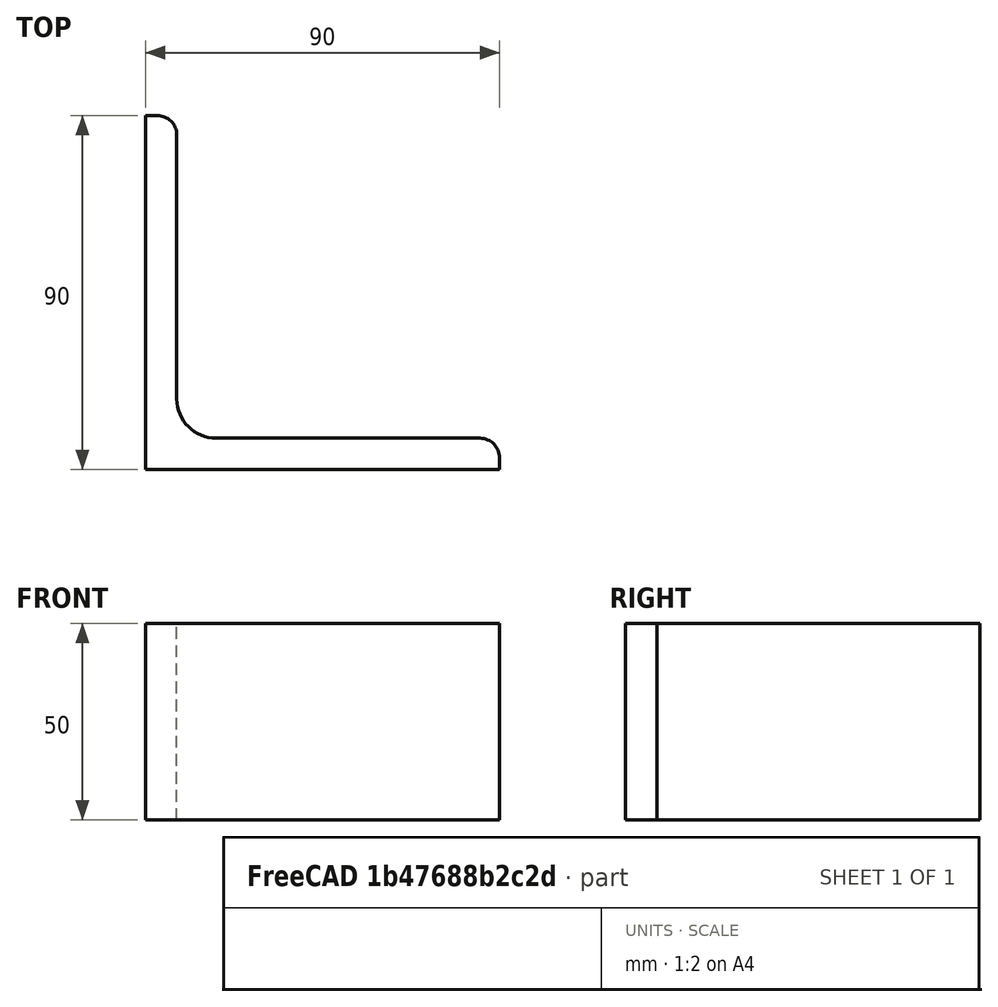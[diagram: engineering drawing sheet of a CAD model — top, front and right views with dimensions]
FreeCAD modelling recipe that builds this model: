
FCSTD DOCUMENT  (FreeCAD 0.15R4671 (Git))
Label: Angle Bar L90x90x8 EN10056 S235JR
License: All rights reserved
LicenseURL: http://en.wikipedia.org/wiki/All_rights_reserved
objects: Sketcher::SketchObject×1, Part::Extrusion×1
note: 2 computed .brp shape members not serialized (recipe doc carries the construction recipe); baked Part::Feature solids carry a one-line shape summary decoded from their .brp

FEATURE [Sketcher::SketchObject] Sketch
  sketch-geometry (9):
    g0: LineSegment StartX=0 StartY=0 StartZ=0 EndX=90 EndY=0 EndZ=0
    g1: LineSegment StartX=90 StartY=0 StartZ=0 EndX=90 EndY=3 EndZ=0
    g2: LineSegment StartX=85 StartY=8 StartZ=0 EndX=18 EndY=8 EndZ=0
    g3: LineSegment StartX=0 StartY=0 StartZ=0 EndX=0 EndY=90 EndZ=0
    g4: LineSegment StartX=0 StartY=90 StartZ=0 EndX=3 EndY=90 EndZ=0
    g5: LineSegment StartX=8 StartY=85 StartZ=0 EndX=8 EndY=18 EndZ=0
    g6: ArcOfCircle CenterX=18 CenterY=18 CenterZ=0 NormalX=0 NormalY=0 NormalZ=1 Radius=10 StartAngle=3.14159 EndAngle=4.71239
    g7: ArcOfCircle CenterX=3 CenterY=85 CenterZ=0 NormalX=0 NormalY=0 NormalZ=1 Radius=5 StartAngle=0 EndAngle=1.5708
    g8: ArcOfCircle CenterX=85 CenterY=3 CenterZ=0 NormalX=0 NormalY=0 NormalZ=1 Radius=5 StartAngle=0 EndAngle=1.5708
  constraints (23):
    c: Coincident(g0,g-1)
    c: Horizontal(g0)
    c: Coincident(g1,g0)
    c: Vertical(g1)
    c: Horizontal(g2)
    c: Coincident(g3,g-1)
    c: Vertical(g3)
    c: Coincident(g4,g3)
    c: Horizontal(g4)
    c: Vertical(g5)
    c: Tangent(g5,g6) = -1.5708
    c: Tangent(g2,g6) = 1.5708
    c: Tangent(g4,g7) = 1.5708
    c: Tangent(g5,g7) = 1.5708
    c: Tangent(g2,g8) = -1.5708
    c: Tangent(g1,g8) = -1.5708
    c: DistanceX(g0) = 90
    c: DistanceY(g3) = 90
    c: DistanceY(g0,g2) = 8
    c: DistanceX(g3,g5) = 8
    c: Radius(g6) = 10
    c: Radius(g8) = 5
    c: Radius(g7) = 5
FEATURE [Part::Extrusion] Extrude  label="Angle Bar L90x90x8 EN10056 S235JR"
  Base = -> Sketch
  Dir = (0,0,50)
  Solid = true
